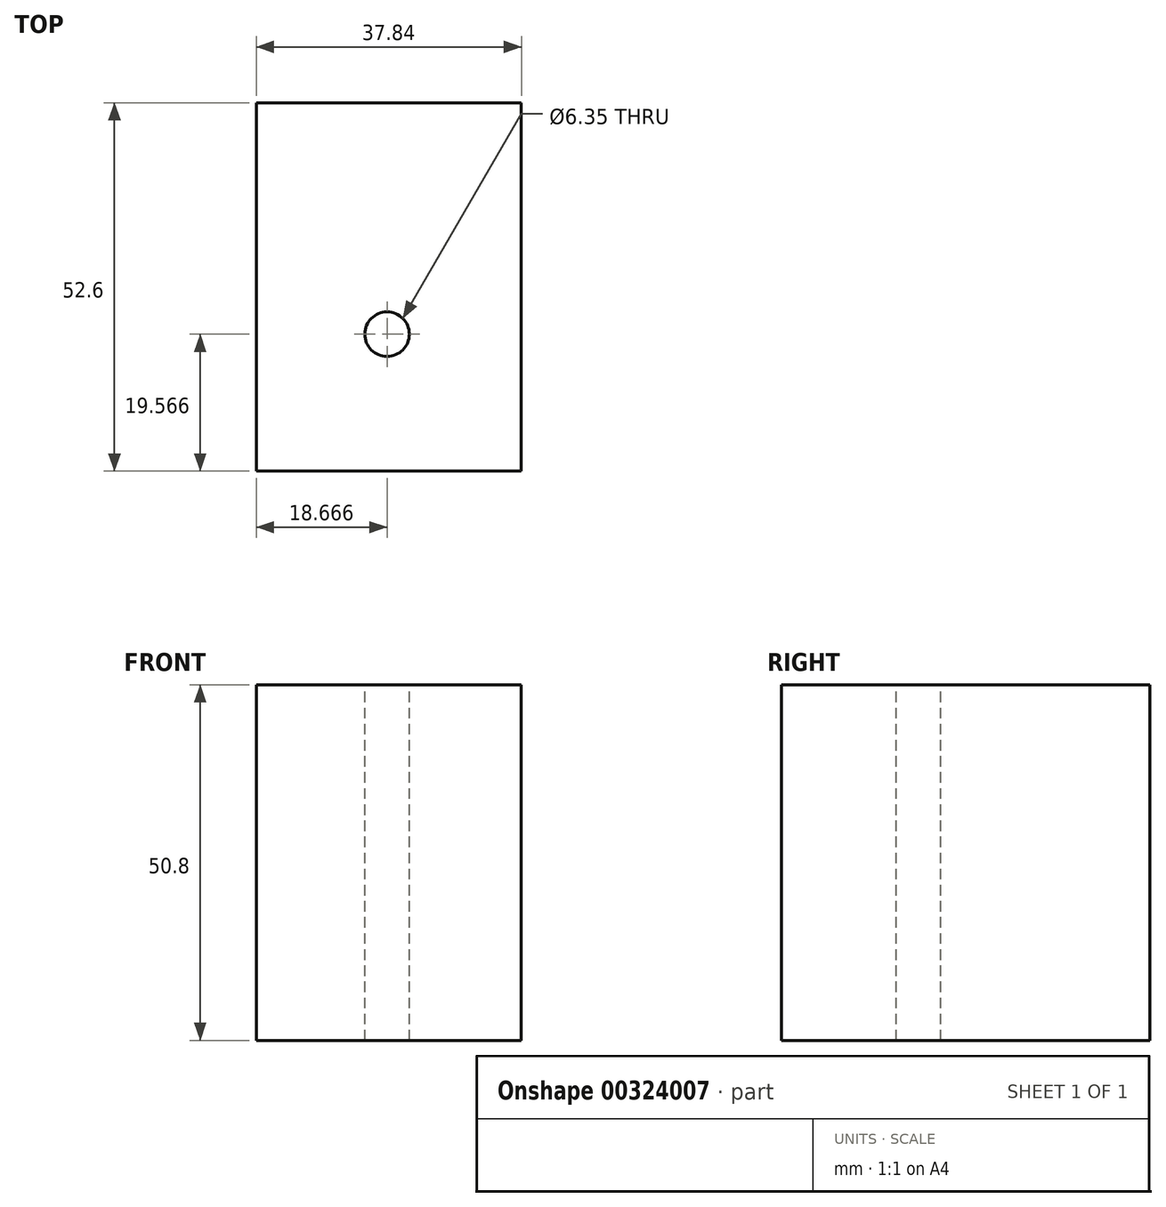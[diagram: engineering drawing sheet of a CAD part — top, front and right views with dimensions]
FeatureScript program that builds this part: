
annotation { "Feature Type Name" : "Feature", "Feature Type Description" : "" }
export const myFeature = defineFeature(function(context is Context, id is Id, definition is map)
    precondition{}
    {
        {
            var Q0;
            Q0=qCreatedBy(makeId("Top.planeOp"),FACE);
            var sketch = newSketch(context, id + "F0", { "sketchPlane" : qUnion([Q0])});
            skLineSegment(sketch, "E0.bottom", {"start": v(0, 0) * mm, "end": v(37.84, 0) * mm});
            skLineSegment(sketch, "E0.top", {"start": v(0, 52.6) * mm, "end": v(37.84, 52.6) * mm});
            skLineSegment(sketch, "E0.left", {"start": v(0, 0) * mm, "end": v(0, 52.6) * mm});
            skLineSegment(sketch, "E0.right", {"start": v(37.84, 0) * mm, "end": v(37.84, 52.6) * mm});
            skSolve(sketch);
        }
        {
            var Q0;
            Q0=makeQuery(id+"F0.imprint","IMPRINT",FACE,{"disambiguationData":[TD([[makeQuery(id+"F0.imprint","IMPRINT",EDGE,{"derivedFrom":sQuery(id+"F0.wireOp",EDGE,"E0.bottom")}),1.0]])]});
            extrude(context, id + "F1", {"entities" : qUnion([Q0]), "depth" : 50.8 * mm});
        }
        {
            var Q0;
            Q0=makeQuery(id+"F1.opExtrude","CAP_FACE",FACE,{"disambiguationData":[OSD([sQuery(id+"F0.wireOp",EDGE,"E0.bottom"),sQuery(id+"F0.wireOp",EDGE,"E0.top"),sQuery(id+"F0.wireOp",EDGE,"E0.left"),sQuery(id+"F0.wireOp",EDGE,"E0.right")])],"isStart":false});
            var sketch = newSketch(context, id + "F2", { "sketchPlane" : qUnion([Q0])});
            skCircle(sketch, "E1", {"center": v(18.67, 19.57) * mm, "radius": 11.61 * mm});
            skSolve(sketch);
        }
        {
            var Q0;
            Q0=sQuery(id+"F2.wireOp",VERTEX,"E1.center");
            var Q1;
            Q1=makeQuery(id+"F1.opExtrude","SWEPT_BODY",BODY,{"disambiguationData":[OSD([sQuery(id+"F0.wireOp",EDGE,"E0.bottom"),sQuery(id+"F0.wireOp",EDGE,"E0.top"),sQuery(id+"F0.wireOp",EDGE,"E0.left"),sQuery(id+"F0.wireOp",EDGE,"E0.right")])]});
            hole(context, id + "F3", {"style" : HoleStyle.SIMPLE, "endStyle" : HoleEndStyle.THROUGH, "holeDiameter" : 6.35 * mm, "tappedDepth" : 12.7 * mm, "tapClearance" : 3, "locations" : qUnion([Q0]), "scope" : qUnion([Q1])});
        }
    });
